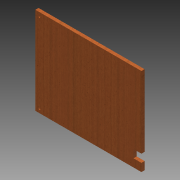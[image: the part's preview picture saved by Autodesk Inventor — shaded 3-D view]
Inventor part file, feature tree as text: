
AUTODESK INVENTOR PART (.ipt)
format: ipt  version: 2015 SP1 (Build 190203100, 203)  size: 103,936 bytes
history: native  units: in
note: dims shown in document units (in); Inventor stores cm internally (conversion verified against a paired STEP export)
features: other x3, sketch x2
ambient origin geometry x8: Origin, YZ Plane, XZ Plane, XY Plane, X Axis, Y Axis, Z Axis, Center Point
bodies: Solid1 (feature_tree)
feature tree (5):
  other  "top plate.ipt"
  other  "Solid1::top plate.ipt"
  other  "TaggingFeature1"
  sketch  "Sketch1"  dims[d0=0.3937in]
  sketch  "Sketch2"
